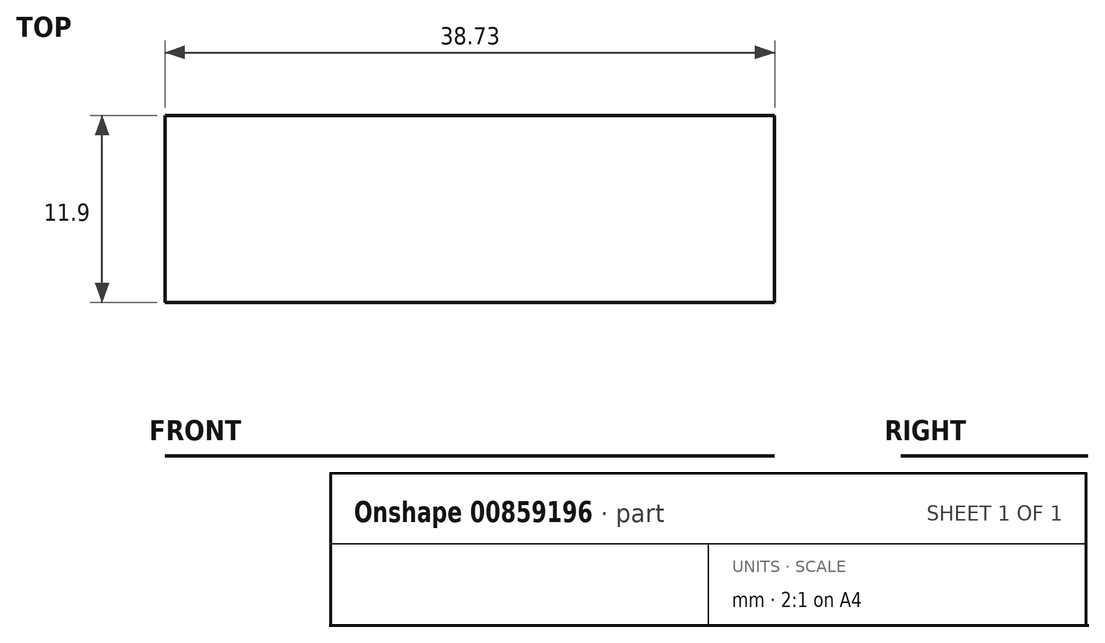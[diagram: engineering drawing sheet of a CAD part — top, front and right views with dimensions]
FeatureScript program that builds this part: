
annotation { "Feature Type Name" : "Feature", "Feature Type Description" : "" }
export const myFeature = defineFeature(function(context is Context, id is Id, definition is map)
    precondition{}
    {
        {
            var Q0;
            Q0=qCreatedBy(makeId("Right.planeOp"),FACE);
            var sketch = newSketch(context, id + "F0", { "sketchPlane" : qUnion([Q0])});
            skLineSegment(sketch, "E0", {"start": v(-11.9, 0) * mm, "end": v(0, 0) * mm});
            skSolve(sketch);
        }
        {
            var Q0;
            Q0=sQuery(id+"F0.wireOp",EDGE,"E0");
            extrude(context, id + "F1", {"bodyType" : ToolBodyType.SURFACE, "surfaceEntities" : qUnion([Q0]), "depth" : 38.73 * mm, "offsetDistance" : 25.4 * mm});
        }
    });
